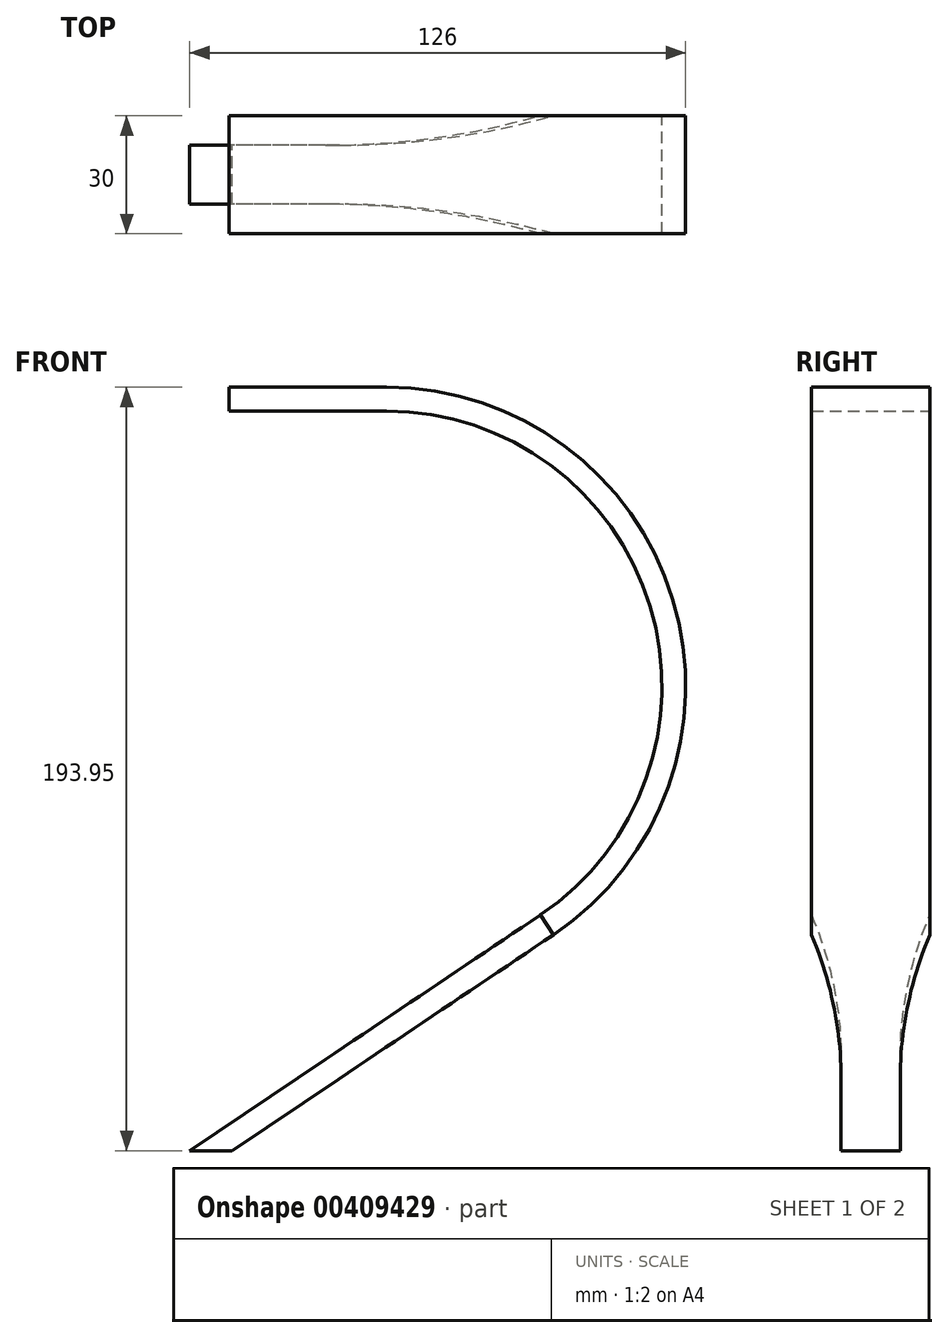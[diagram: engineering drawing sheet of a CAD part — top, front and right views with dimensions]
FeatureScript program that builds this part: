
annotation { "Feature Type Name" : "Feature", "Feature Type Description" : "" }
export const myFeature = defineFeature(function(context is Context, id is Id, definition is map)
    precondition{}
    {
        {
            var Q0;
            Q0=qCreatedBy(makeId("Front.planeOp"),FACE);
            var sketch = newSketch(context, id + "F0", { "sketchPlane" : qUnion([Q0])});
            skArc(sketch, "E0", {"start": v(39.05, 59.86) * mm, "mid": v(66.96, 138.36) * mm, "end": v(0, 187.95) * mm});
            skLineSegment(sketch, "E1", {"start": v(-40, 187.95) * mm, "end": v(0, 187.95) * mm});
            skLineSegment(sketch, "E2", {"start": v(0, 0) * mm, "end": v(0, 336.73) * mm, "construction": true});
            skLineSegment(sketch, "E3", {"start": v(-40, 193.95) * mm, "end": v(-40, 187.95) * mm});
            skLineSegment(sketch, "E4", {"start": v(-50, 38.58) * mm, "end": v(-50, -30.22) * mm, "construction": true});
            skLineSegment(sketch, "E5", {"start": v(-50, 0) * mm, "end": v(39.05, 59.86) * mm});
            skLineSegment(sketch, "E6.0", {"start": v(-40, 193.95) * mm, "end": v(0, 193.95) * mm});
            skArc(sketch, "E6.1", {"start": v(42.4, 54.88) * mm, "mid": v(72.7, 140.11) * mm, "end": v(0, 193.95) * mm});
            skLineSegment(sketch, "E6.2", {"start": v(-39.24, 0) * mm, "end": v(42.4, 54.88) * mm});
            skLineSegment(sketch, "E7", {"start": v(-50, 0) * mm, "end": v(-39.24, 0) * mm});
            skLineSegment(sketch, "E8", {"start": v(50, 81.17) * mm, "end": v(50, -97.2) * mm, "construction": true});
            skSolve(sketch);
        }
        {
            var Q0;
            Q0=qSketchRegion(id+"F0",true);
            extrude(context, id + "F1", {"entities" : qUnion([Q0]), "depth" : 30 * mm, "offsetDistance" : 25 * mm, "symmetric" : true});
        }
        {
            var Q0;
            Q0=makeQuery(id+"F1.opExtrude","SWEPT_FACE",FACE,{"disambiguationData":[OSD([sQuery(id+"F0.wireOp",EDGE,"E5")])]});
            var sketch = newSketch(context, id + "F2", { "sketchPlane" : qUnion([Q0])});
            skLineSegment(sketch, "E9", {"start": v(6.57, -7.5) * mm, "end": v(-111.74, -7.5) * mm});
            skArc(sketch, "E10", {"start": v(65.8, -15) * mm, "mid": v(33.11, -9.37) * mm, "end": v(0, -7.5) * mm});
            skPoint(sketch, "E10.endSnap0", {"position": v(6.57, -7.5) * mm});
            skLineSegment(sketch, "E11", {"start": v(65.8, -15) * mm, "end": v(65.8, -33.44) * mm});
            skLineSegment(sketch, "E12", {"start": v(65.8, -33.44) * mm, "end": v(-111.74, -33.44) * mm});
            skLineSegment(sketch, "E13", {"start": v(-111.74, -33.44) * mm, "end": v(-111.74, -7.5) * mm});
            skPoint(sketch, "E14.orphan", {"position": v(124.89, -7.5) * mm});
            skLineSegment(sketch, "E15", {"start": v(-84.98, 0) * mm, "end": v(112.1, 0) * mm, "construction": true});
            skLineSegment(sketch, "E16.MirrorCS", {"start": v(6.57, 7.5) * mm, "end": v(-111.74, 7.5) * mm});
            skArc(sketch, "E17.MirrorCS", {"start": v(65.8, 15) * mm, "mid": v(33.11, 9.37) * mm, "end": v(0, 7.5) * mm});
            skLineSegment(sketch, "E18.MirrorCS", {"start": v(65.8, 33.44) * mm, "end": v(-111.74, 33.44) * mm});
            skLineSegment(sketch, "E19.MirrorCS", {"start": v(65.8, 15) * mm, "end": v(65.8, 33.44) * mm});
            skLineSegment(sketch, "E20.MirrorCS", {"start": v(-111.74, 33.44) * mm, "end": v(-111.74, 7.5) * mm});
            skSolve(sketch);
        }
        {
            var Q0;
            Q0 = qSketchRegion(id + "F2", true);
            extrude(context, id + "F3", {"entities" : qUnion([Q0]), "operationType" : NewBodyOperationType.REMOVE, "oppositeDirection" : true, "depth" : 10 * mm, "offsetDistance" : 25 * mm});
        }
    });
